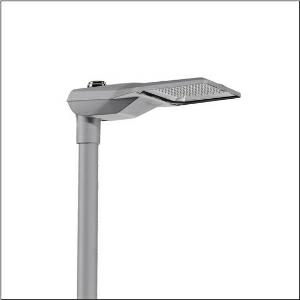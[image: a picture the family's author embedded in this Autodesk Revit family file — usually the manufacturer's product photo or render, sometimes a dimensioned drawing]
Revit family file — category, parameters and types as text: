
# Revit family: streetlight_sl_21_midi___st0_8a_5xe7c47n08mb_cd2e
name_source: partatom
category: Lighting Fixtures
units: mm (PartAtom-declared; Revit-internal decimal feet)

## family parameters
Cut with Voids When Loaded = No
Host = Face
Light Source = No
Part Type = Normal
Room Calculation Point = No
Round Connector Dimension = Use Diameter
Shared = No

## types (1)
- --- (1 x LED, 20180 lm, 147 W, 4000K)
    Apparent Load = 147 VA
    CIE Flux Codes = 38 75 97 100 100
    Color Rendering = 70
    Color Temperature = 4000K
    Default Elevation = 1800 mm
    Description = Streetlight SL 21 midi, mast luminaire, primary light control with lens, of PMMA, primary optical cover: cover, of toughened safety glass, transparent, light distribution: ST0.8a, light emission: direct distribution, primary light characteristic: asymmetric, installation type: side-entry, LED, 3G 2.5mm², High Power LED, rated luminous flux: 20.180lm, luminous efficacy: 137lm/W, light colour: 740, colour temperature: 4000K, control gear: NEMA (7pin), control: overheat protection, pre-setting: linear dimming characteristic, constant luminous flux control, time-dependent luminous flux control, flexible luminous flux parameterisation, mains connection: 220..240V, AC, 50/60Hz, connection cable pre-assembled, cable length: 12,5m, wiring characteristics: H05VV-F, start of lifetime: 147W, end of service life: 155W, reduction: 65W, luminaire housing, of diecast aluminium (EN AC-44300), powder-coated, Siteco® metallic grey (DB 702S), corrosivity category C5 mid according to DIN EN ISO 12944, multi-level sealing system, sealing non-destructively replaceable, inclination adjustable: 0°, 5°, 10°, 15°, length: 644mm, width: 335mm, height: 110mm, spigot size: 42mm (side-entry), mounting height: 4..8m, protection rating (complete): IP66, insulation class (complete): insulation class I (protective earthing), certification: CE, ENEC, ENEC+, VDE, impact resistance: IK10, permissible operating ambient temperature for outdoor applications: -40..+50°C, standard-compliant lighting for roads and squares, packaging unit: 1 piece

Light Distribution: ST0.8a
    Height = 111 mm
    Lamp = 1 x LED
    Lamp Light Flux = 20180 lm
    Lamp Power = 147 W
    Lamp count = 1
    Length = 644 mm
    Luminous efficacy = 137 lm/W
    Manufacturer = Siteco
    ModVariant = No
    Model = 5XE7C47N08MB
    Number of Poles = 1
    OnlyDefault = Yes
    Power Factor = 1
    Product Name = Streetlight SL 21 midi | ST0.8a
    Product group = mast luminaire | pylon top
    ProductGroupID = 6100
    Protection Class = Protection class I
    Protection Degree = IP 66
    RLX_Detail_Level = 1
    RLX_Emergency_Light_Flux = 0 lm
    RLX_Emergency_Type = 0
    RLX_Emergency_Type_DB = No
    RlxData = <blob elided: 26569 chars, md5=673aa7c8>
    Socket = socket
    Standby Power = 0 W
    System Light Flux = 20180 lm
    System Power = 147 W
    Type Comments = factory setting: luminous flux: 100 % | dim-lin: 254 | 750 mA
    Type Image = l_1294377.jpg
    URL = http://relux.com
    VarID = @adj_155471
    Voltage = 0 V
    Weight = 0.00 kg
    Width = 336 mm

## geometry (parser evidence)
native form markers: Blend x4, Sweep x12
no freeform markers — native parametric forms only
